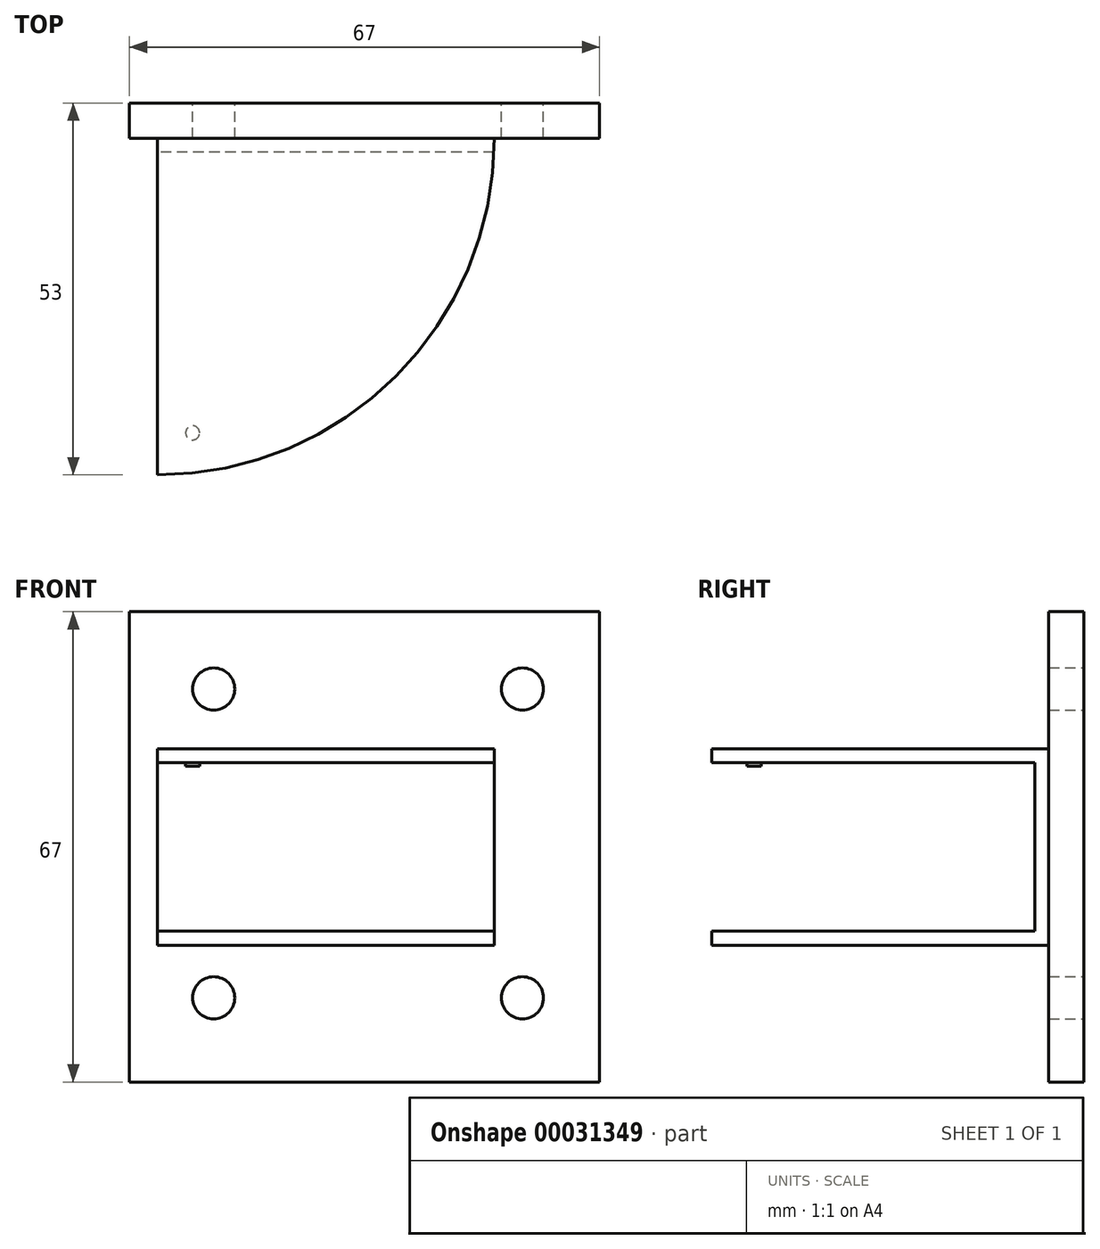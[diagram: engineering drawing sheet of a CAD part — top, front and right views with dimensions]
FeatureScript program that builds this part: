
annotation { "Feature Type Name" : "Feature", "Feature Type Description" : "" }
export const myFeature = defineFeature(function(context is Context, id is Id, definition is map)
    precondition{}
    {
        {
            var Q0;
            Q0=qCreatedBy(makeId("Top.planeOp"),FACE);
            var sketch = newSketch(context, id + "F0", { "sketchPlane" : qUnion([Q0])});
            skLineSegment(sketch, "E0.bottom", {"start": v(-5, 42) * mm, "end": v(43, 42) * mm});
            skLineSegment(sketch, "E0.left", {"start": v(-5, 42) * mm, "end": v(-5, -6) * mm});
            skArc(sketch, "E1", {"start": v(-5, -6) * mm, "mid": v(28.94, 8.06) * mm, "end": v(43, 42) * mm});
            skSolve(sketch);
        }
        {
            var Q0;
            Q0 = qSketchRegion(id + "F0", true);
            extrude(context, id + "F1", {"entities" : qUnion([Q0]), "endBound" : BoundingType.SYMMETRIC, "depth" : 28 * mm});
        }
        {
            var Q0;
            Q0=makeQuery(id+"F1.opExtrude","SWEPT_FACE",FACE,{"disambiguationData":[OSD([sQuery(id+"F0.wireOp",EDGE,"E0.left")])]});
            var sketch = newSketch(context, id + "F2", { "sketchPlane" : qUnion([Q0])});
            skLineSegment(sketch, "E2.bottom", {"start": v(6, 12) * mm, "end": v(-40, 12) * mm});
            skLineSegment(sketch, "E2.top", {"start": v(6, -12) * mm, "end": v(-40, -12) * mm});
            skLineSegment(sketch, "E2.left", {"start": v(6, 12) * mm, "end": v(6, -12) * mm});
            skLineSegment(sketch, "E2.right", {"start": v(-40, 12) * mm, "end": v(-40, -12) * mm});
            skSolve(sketch);
        }
        {
            var Q0;
            Q0 = qSketchRegion(id + "F2", true);
            extrude(context, id + "F3", {"entities" : qUnion([Q0]), "operationType" : NewBodyOperationType.REMOVE, "oppositeDirection" : true, "depth" : 55 * mm});
        }
        {
            var Q0;
            Q0=makeQuery(id+"F1.opExtrude","CAP_FACE",FACE,{"disambiguationData":[OSD([sQuery(id+"F0.wireOp",EDGE,"E0.bottom"),sQuery(id+"F0.wireOp",EDGE,"E0.left"),sQuery(id+"F0.wireOp",EDGE,"E1")])],"isStart":false});
            var sketch = newSketch(context, id + "F4", { "sketchPlane" : qUnion([Q0])});
            skCircle(sketch, "E3", {"center": v(0, 0) * mm, "radius": 1 * mm});
            skSolve(sketch);
        }
        {
            var Q0;
            Q0 = qSketchRegion(id + "F4", true);
            extrude(context, id + "F5", {"entities" : qUnion([Q0]), "operationType" : NewBodyOperationType.ADD, "oppositeDirection" : true, "depth" : 2.5 * mm});
        }
        {
            var Q0;
            Q0=makeQuery(id+"F1.opExtrude","SWEPT_FACE",FACE,{"disambiguationData":[OSD([sQuery(id+"F0.wireOp",EDGE,"E0.bottom")])]});
            var sketch = newSketch(context, id + "F6", { "sketchPlane" : qUnion([Q0])});
            skLineSegment(sketch, "E4.bottom", {"start": v(9, 33.5) * mm, "end": v(-58, 33.5) * mm});
            skLineSegment(sketch, "E4.top", {"start": v(9, -33.5) * mm, "end": v(-58, -33.5) * mm});
            skLineSegment(sketch, "E4.left", {"start": v(9, 33.5) * mm, "end": v(9, -33.5) * mm});
            skLineSegment(sketch, "E4.right", {"start": v(-58, 33.5) * mm, "end": v(-58, -33.5) * mm});
            skSolve(sketch);
        }
        {
            var Q0;
            Q0 = qSketchRegion(id + "F6", true);
            extrude(context, id + "F7", {"entities" : qUnion([Q0]), "operationType" : NewBodyOperationType.ADD, "depth" : 5 * mm});
        }
        {
            var Q0;
            Q0=makeQuery(id+"F7.opExtrude","CAP_FACE",FACE,{"disambiguationData":[OSD([sQuery(id+"F6.wireOp",EDGE,"E4.bottom"),sQuery(id+"F6.wireOp",EDGE,"E4.top"),sQuery(id+"F6.wireOp",EDGE,"E4.left"),sQuery(id+"F6.wireOp",EDGE,"E4.right")])],"isStart":false});
            var sketch = newSketch(context, id + "F8", { "sketchPlane" : qUnion([Q0])});
            skCircle(sketch, "E5", {"center": v(-47, 22.5) * mm, "radius": 3 * mm});
            skCircle(sketch, "E6", {"center": v(-3, 22.5) * mm, "radius": 3 * mm});
            skCircle(sketch, "E7", {"center": v(-47, -21.5) * mm, "radius": 3 * mm});
            skCircle(sketch, "E8", {"center": v(-3, -21.5) * mm, "radius": 3 * mm});
            skSolve(sketch);
        }
        {
            var Q0;
            Q0 = qSketchRegion(id + "F8", true);
            extrude(context, id + "F9", {"entities" : qUnion([Q0]), "operationType" : NewBodyOperationType.REMOVE, "oppositeDirection" : true, "depth" : 25 * mm});
        }
    });
